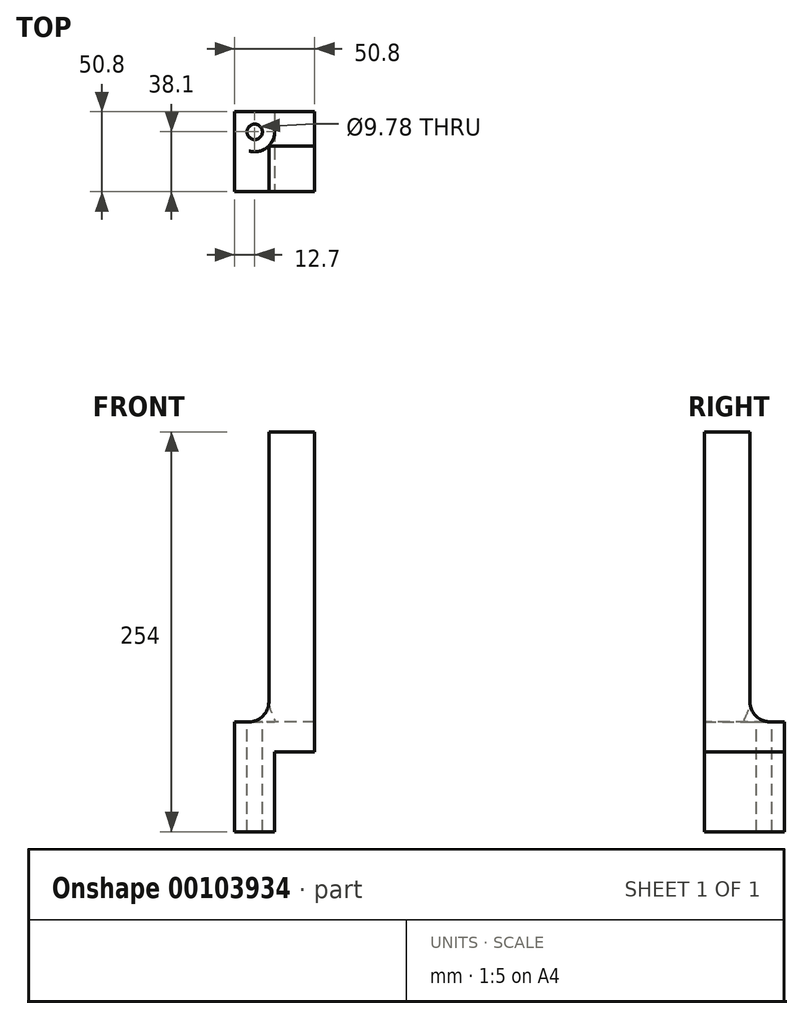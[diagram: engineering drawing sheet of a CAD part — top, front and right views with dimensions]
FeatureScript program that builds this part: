
annotation { "Feature Type Name" : "Feature", "Feature Type Description" : "" }
export const myFeature = defineFeature(function(context is Context, id is Id, definition is map)
    precondition{}
    {
        {
            var Q0;
            Q0=qCreatedBy(makeId("Top.planeOp"),FACE);
            var sketch = newSketch(context, id + "F0", { "sketchPlane" : qUnion([Q0])});
            skLineSegment(sketch, "E0.bottom", {"start": v(0, 0) * mm, "end": v(-50.8, 0) * mm});
            skLineSegment(sketch, "E0.top", {"start": v(0, 50.8) * mm, "end": v(-50.8, 50.8) * mm});
            skLineSegment(sketch, "E0.left", {"start": v(0, 0) * mm, "end": v(0, 50.8) * mm});
            skLineSegment(sketch, "E0.right", {"start": v(-50.8, 0) * mm, "end": v(-50.8, 50.8) * mm});
            skSolve(sketch);
        }
        {
            var Q0;
            Q0=qSketchRegion(id+"F0",true);
            extrude(context, id + "F1", {"entities" : qUnion([Q0]), "depth" : 254 * mm});
        }
        {
            var Q0;
            Q0=makeQuery(id+"F1.opExtrude","SWEPT_FACE",FACE,{"disambiguationData":[OSD([sQuery(id+"F0.wireOp",EDGE,"E0.right")])]});
            var sketch = newSketch(context, id + "F2", { "sketchPlane" : qUnion([Q0])});
            skLineSegment(sketch, "E1", {"start": v(-50.8, 69.85) * mm, "end": v(-41.82, 69.85) * mm});
            skArc(sketch, "E2", {"start": v(-41.82, 69.85) * mm, "mid": v(-32.84, 73.57) * mm, "end": v(-29.12, 82.55) * mm});
            skLineSegment(sketch, "E3", {"start": v(-29.12, 82.55) * mm, "end": v(-29.12, 254) * mm});
            skLineSegment(sketch, "E4", {"start": v(-29.12, 254) * mm, "end": v(-50.8, 254) * mm});
            skLineSegment(sketch, "E5", {"start": v(-50.8, 254) * mm, "end": v(-50.8, 69.85) * mm});
            skSolve(sketch);
        }
        {
            var Q0;
            Q0=qSketchRegion(id+"F2",true);
            extrude(context, id + "F3", {"entities" : qUnion([Q0]), "operationType" : NewBodyOperationType.REMOVE, "endBound" : BoundingType.THROUGH_ALL, "oppositeDirection" : true, "depth" : 25.4 * mm});
        }
        {
            var Q0;
            Q0=makeQuery(id+"F1.opExtrude","SWEPT_FACE",FACE,{"disambiguationData":[OSD([sQuery(id+"F0.wireOp",EDGE,"E0.top")])]});
            var sketch = newSketch(context, id + "F4", { "sketchPlane" : qUnion([Q0])});
            skLineSegment(sketch, "E6", {"start": v(41.82, 69.85) * mm, "end": v(50.8, 69.85) * mm});
            skLineSegment(sketch, "E7", {"start": v(50.8, 69.85) * mm, "end": v(50.8, 254) * mm});
            skLineSegment(sketch, "E8", {"start": v(50.8, 254) * mm, "end": v(29.12, 254) * mm});
            skLineSegment(sketch, "E9", {"start": v(29.12, 254) * mm, "end": v(29.12, 82.55) * mm});
            skArc(sketch, "E10", {"start": v(29.12, 82.55) * mm, "mid": v(32.84, 73.57) * mm, "end": v(41.82, 69.85) * mm});
            skSolve(sketch);
        }
        {
            var Q0;
            Q0=qSketchRegion(id+"F4",true);
            extrude(context, id + "F5", {"entities" : qUnion([Q0]), "operationType" : NewBodyOperationType.REMOVE, "endBound" : BoundingType.THROUGH_ALL, "oppositeDirection" : true, "depth" : 25.4 * mm});
        }
        {
            var Q0;
            Q0=makeQuery(id+"F5.boolean.opBoolean","MERGE",FACE,{"derivedFrom":[makeQuery(id+"F3.boolean.opBoolean","COPY",FACE,{"derivedFrom":makeQuery(id+"F3.opExtrude","SWEPT_FACE",FACE,{"disambiguationData":[OSD([sQuery(id+"F2.wireOp",EDGE,"E1")])]})}),makeQuery(id+"F5.opExtrude","SWEPT_FACE",FACE,{"disambiguationData":[OSD([sQuery(id+"F4.wireOp",EDGE,"E6")])]})]});
            var sketch = newSketch(context, id + "F6", { "sketchPlane" : qUnion([Q0])});
            skCircle(sketch, "E11", {"center": v(-38.1, 38.1) * mm, "radius": 12.7 * mm});
            skSolve(sketch);
        }
        {
            var Q0;
            Q0=qSketchRegion(id+"F6",true);
            extrude(context, id + "F7", {"entities" : qUnion([Q0]), "operationType" : NewBodyOperationType.REMOVE, "depth" : 25.4 * mm});
        }
        {
            var Q0;
            Q0=makeQuery(id+"F1.opExtrude","SWEPT_FACE",FACE,{"disambiguationData":[OSD([sQuery(id+"F0.wireOp",EDGE,"E0.bottom")])]});
            var sketch = newSketch(context, id + "F8", { "sketchPlane" : qUnion([Q0])});
            skLineSegment(sketch, "E12.bottom", {"start": v(0, 0) * mm, "end": v(-25.4, 0) * mm});
            skLineSegment(sketch, "E12.top", {"start": v(0, 50.8) * mm, "end": v(-25.4, 50.8) * mm});
            skLineSegment(sketch, "E12.left", {"start": v(0, 0) * mm, "end": v(0, 50.8) * mm});
            skLineSegment(sketch, "E12.right", {"start": v(-25.4, 0) * mm, "end": v(-25.4, 50.8) * mm});
            skSolve(sketch);
        }
        {
            var Q0;
            Q0 = qSketchRegion(id + "F8", true);
            extrude(context, id + "F9", {"entities" : qUnion([Q0]), "operationType" : NewBodyOperationType.REMOVE, "endBound" : BoundingType.THROUGH_ALL, "oppositeDirection" : true, "depth" : 25.4 * mm});
        }
        {
            var Q0;
            Q0=makeQuery(id+"F7.boolean.opBoolean","MERGE",FACE,{"derivedFrom":[makeQuery(id+"F5.boolean.opBoolean","MERGE",FACE,{"derivedFrom":[makeQuery(id+"F3.boolean.opBoolean","COPY",FACE,{"derivedFrom":makeQuery(id+"F3.opExtrude","SWEPT_FACE",FACE,{"disambiguationData":[OSD([sQuery(id+"F2.wireOp",EDGE,"E1")])]})}),makeQuery(id+"F5.opExtrude","SWEPT_FACE",FACE,{"disambiguationData":[OSD([sQuery(id+"F4.wireOp",EDGE,"E6")])]})]}),makeQuery(id+"F7.opExtrude","CAP_FACE",FACE,{"disambiguationData":[OSD([sQuery(id+"F6.wireOp",EDGE,"E11")])],"isStart":true})]});
            var sketch = newSketch(context, id + "F10", { "sketchPlane" : qUnion([Q0])});
            skCircle(sketch, "E13", {"center": v(-38.1, 38.1) * mm, "radius": 4.89 * mm});
            skSolve(sketch);
        }
        {
            var Q0;
            Q0 = qSketchRegion(id + "F10", true);
            extrude(context, id + "F11", {"entities" : qUnion([Q0]), "operationType" : NewBodyOperationType.REMOVE, "endBound" : BoundingType.THROUGH_ALL, "oppositeDirection" : true, "depth" : 25.4 * mm});
        }
    });
